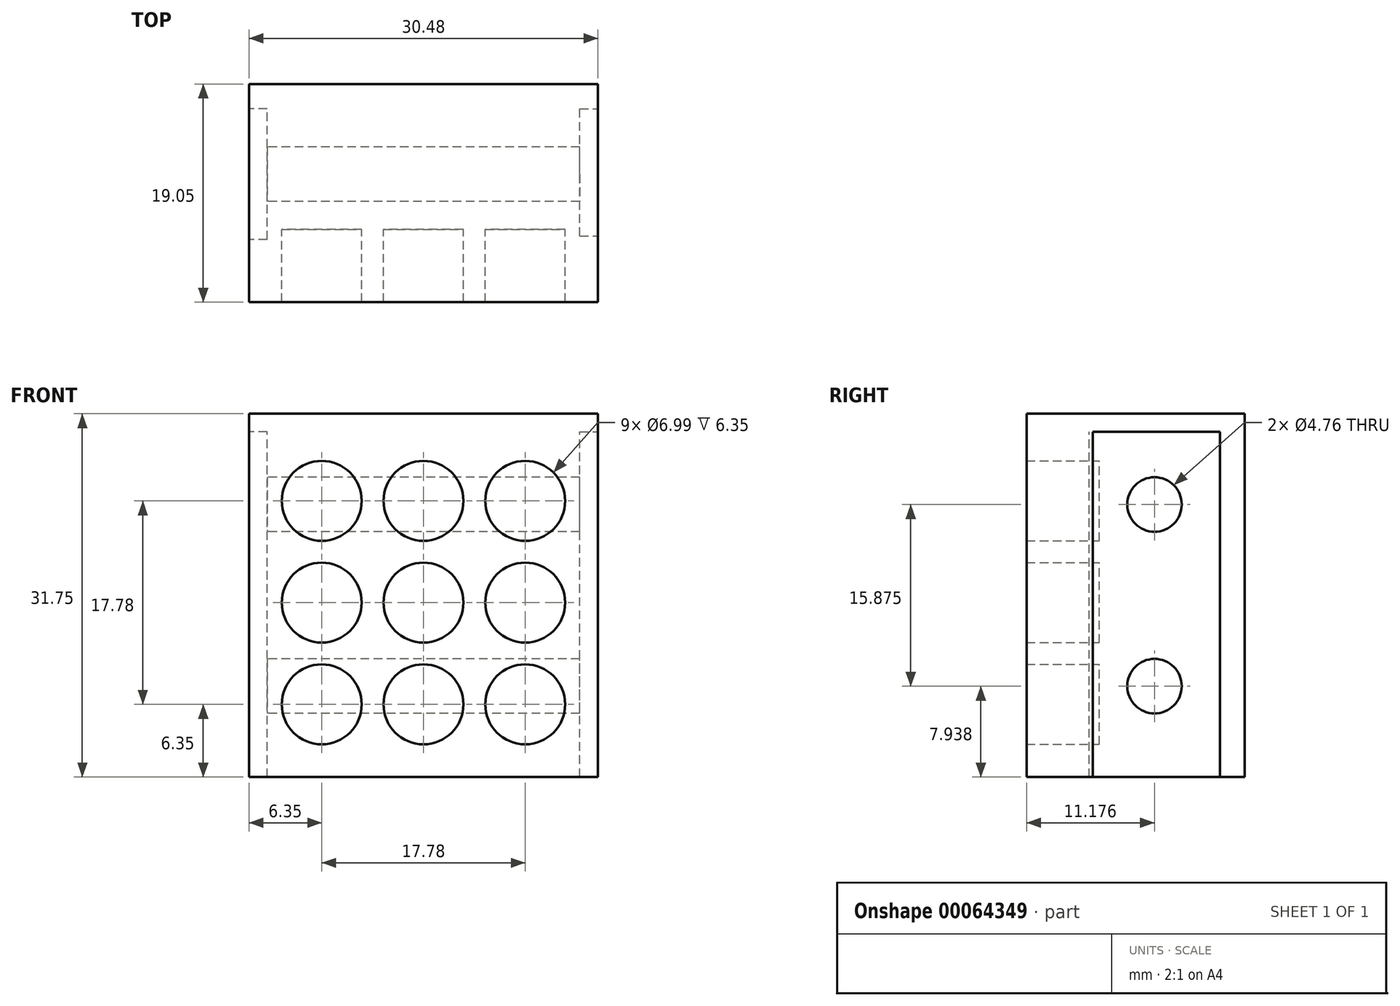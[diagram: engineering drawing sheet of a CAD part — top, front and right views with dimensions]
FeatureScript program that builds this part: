
annotation { "Feature Type Name" : "Feature", "Feature Type Description" : "" }
export const myFeature = defineFeature(function(context is Context, id is Id, definition is map)
    precondition{}
    {
        {
            var Q0;
            Q0=qCreatedBy(makeId("Front.planeOp"),FACE);
            var sketch = newSketch(context, id + "F0", { "sketchPlane" : qUnion([Q0])});
            skLineSegment(sketch, "E0.bottom", {"start": v(0, 0) * mm, "end": v(-30.48, 0) * mm});
            skLineSegment(sketch, "E0.top", {"start": v(0, 31.75) * mm, "end": v(-30.48, 31.75) * mm});
            skLineSegment(sketch, "E0.left", {"start": v(0, 0) * mm, "end": v(0, 31.75) * mm});
            skLineSegment(sketch, "E0.right", {"start": v(-30.48, 0) * mm, "end": v(-30.48, 31.75) * mm});
            skLineSegment(sketch, "E1", {"start": v(-6.35, 31.75) * mm, "end": v(-6.35, 0) * mm, "construction": true});
            skLineSegment(sketch, "E2", {"start": v(-15.24, 31.75) * mm, "end": v(-15.24, 0) * mm, "construction": true});
            skLineSegment(sketch, "E3", {"start": v(-30.48, 24.13) * mm, "end": v(0, 24.13) * mm, "construction": true});
            skLineSegment(sketch, "E4", {"start": v(0, 15.24) * mm, "end": v(-30.48, 15.24) * mm, "construction": true});
            skCircle(sketch, "E5", {"center": v(-6.35, 24.13) * mm, "radius": 3.5 * mm});
            skLineSegment(sketch, "E6", {"start": v(-24.13, 31.75) * mm, "end": v(-24.13, 0) * mm, "construction": true});
            skLineSegment(sketch, "E7", {"start": v(-30.48, 6.35) * mm, "end": v(0, 6.35) * mm, "construction": true});
            skCircle(sketch, "E8.0.1.0", {"center": v(-6.35, 15.24) * mm, "radius": 3.5 * mm});
            skCircle(sketch, "E8.0.2.0", {"center": v(-6.35, 6.35) * mm, "radius": 3.5 * mm});
            skCircle(sketch, "E8.1.0.0", {"center": v(-15.24, 24.13) * mm, "radius": 3.5 * mm});
            skCircle(sketch, "E8.1.1.0", {"center": v(-15.24, 15.24) * mm, "radius": 3.5 * mm});
            skCircle(sketch, "E8.1.2.0", {"center": v(-15.24, 6.35) * mm, "radius": 3.5 * mm});
            skCircle(sketch, "E8.2.0.0", {"center": v(-24.13, 24.13) * mm, "radius": 3.5 * mm});
            skCircle(sketch, "E8.2.1.0", {"center": v(-24.13, 15.24) * mm, "radius": 3.5 * mm});
            skCircle(sketch, "E8.2.2.0", {"center": v(-24.13, 6.35) * mm, "radius": 3.5 * mm});
            skLineSegment(sketch, "E8.direction1", {"start": v(-6.35, 24.13) * mm, "end": v(-15.24, 24.13) * mm, "construction": true});
            skLineSegment(sketch, "E8.direction2", {"start": v(-6.35, 24.13) * mm, "end": v(-6.35, 15.24) * mm, "construction": true});
            skSolve(sketch);
        }
        {
            var Q0;
            Q0=makeQuery(id+"F0.imprint","IMPRINT",FACE,{"disambiguationData":[TD([[makeQuery(id+"F0.imprint","IMPRINT",EDGE,{"derivedFrom":sQuery(id+"F0.wireOp",EDGE,"E0.bottom")}),-1.0]])]});
            extrude(context, id + "F1", {"entities" : qUnion([Q0]), "depth" : 6.35 * mm});
        }
        {
            var Q0;
            Q0=makeQuery(id+"F1.opExtrude","CAP_FACE",FACE,{"disambiguationData":[OSD([sQuery(id+"F0.wireOp",EDGE,"E0.bottom"),sQuery(id+"F0.wireOp",EDGE,"E0.top"),sQuery(id+"F0.wireOp",EDGE,"E0.left"),sQuery(id+"F0.wireOp",EDGE,"E0.right"),sQuery(id+"F0.wireOp",EDGE,"E5"),sQuery(id+"F0.wireOp",EDGE,"E8.0.1.0"),sQuery(id+"F0.wireOp",EDGE,"E8.0.2.0"),sQuery(id+"F0.wireOp",EDGE,"E8.1.0.0"),sQuery(id+"F0.wireOp",EDGE,"E8.1.1.0"),sQuery(id+"F0.wireOp",EDGE,"E8.1.2.0"),sQuery(id+"F0.wireOp",EDGE,"E8.2.0.0"),sQuery(id+"F0.wireOp",EDGE,"E8.2.1.0"),sQuery(id+"F0.wireOp",EDGE,"E8.2.2.0")])],"isStart":true});
            var sketch = newSketch(context, id + "F2", { "sketchPlane" : qUnion([Q0])});
            skLineSegment(sketch, "E9.bottom", {"start": v(0, 31.75) * mm, "end": v(30.48, 31.75) * mm});
            skLineSegment(sketch, "E9.top", {"start": v(0, 0) * mm, "end": v(30.48, 0) * mm});
            skLineSegment(sketch, "E9.left", {"start": v(0, 31.75) * mm, "end": v(0, 0) * mm});
            skLineSegment(sketch, "E9.right", {"start": v(30.48, 31.75) * mm, "end": v(30.48, 0) * mm});
            skSolve(sketch);
        }
        {
            var Q0;
            Q0 = qSketchRegion(id + "F2", true);
            extrude(context, id + "F3", {"entities" : qUnion([Q0]), "operationType" : NewBodyOperationType.ADD, "depth" : 12.7 * mm});
        }
        {
            var Q0;
            Q0=makeQuery(id+"F3.boolean.opBoolean","MERGE",FACE,{"derivedFrom":[makeQuery(id+"F1.opExtrude","SWEPT_FACE",FACE,{"disambiguationData":[OSD([sQuery(id+"F0.wireOp",EDGE,"E0.left")])]}),makeQuery(id+"F3.opExtrude","SWEPT_FACE",FACE,{"disambiguationData":[OSD([sQuery(id+"F2.wireOp",EDGE,"E9.left")])]})]});
            var sketch = newSketch(context, id + "F4", { "sketchPlane" : qUnion([Q0])});
            skLineSegment(sketch, "E10.bottom", {"start": v(-0.57, 0) * mm, "end": v(10.54, 0) * mm});
            skLineSegment(sketch, "E10.top", {"start": v(-0.57, 30.16) * mm, "end": v(10.54, 30.16) * mm});
            skLineSegment(sketch, "E10.left", {"start": v(-0.57, 0) * mm, "end": v(-0.57, 30.16) * mm});
            skLineSegment(sketch, "E10.right", {"start": v(10.54, 0) * mm, "end": v(10.54, 30.16) * mm});
            skSolve(sketch);
        }
        {
            var Q0;
            Q0 = qSketchRegion(id + "F4", true);
            extrude(context, id + "F5", {"entities" : qUnion([Q0]), "operationType" : NewBodyOperationType.REMOVE, "oppositeDirection" : true, "depth" : 1.59 * mm});
        }
        {
            var Q0;
            Q0=makeQuery(id+"F3.boolean.opBoolean","MERGE",FACE,{"derivedFrom":[makeQuery(id+"F1.opExtrude","SWEPT_FACE",FACE,{"disambiguationData":[OSD([sQuery(id+"F0.wireOp",EDGE,"E0.right")])]}),makeQuery(id+"F3.opExtrude","SWEPT_FACE",FACE,{"disambiguationData":[OSD([sQuery(id+"F2.wireOp",EDGE,"E9.right")])]})]});
            var sketch = newSketch(context, id + "F6", { "sketchPlane" : qUnion([Q0])});
            skLineSegment(sketch, "E11.bottom", {"start": v(-10.54, 0) * mm, "end": v(0.89, 0) * mm});
            skLineSegment(sketch, "E11.top", {"start": v(-10.54, 30.16) * mm, "end": v(0.89, 30.16) * mm});
            skLineSegment(sketch, "E11.left", {"start": v(-10.54, 0) * mm, "end": v(-10.54, 30.16) * mm});
            skLineSegment(sketch, "E11.right", {"start": v(0.89, 0) * mm, "end": v(0.89, 30.16) * mm});
            skSolve(sketch);
        }
        {
            var Q0;
            Q0 = qSketchRegion(id + "F6", true);
            extrude(context, id + "F7", {"entities" : qUnion([Q0]), "operationType" : NewBodyOperationType.REMOVE, "oppositeDirection" : true, "depth" : 1.59 * mm});
        }
        {
            var Q0;
            Q0=makeQuery(id+"F7.boolean.opBoolean","COPY",FACE,{"derivedFrom":makeQuery(id+"F7.opExtrude","CAP_FACE",FACE,{"disambiguationData":[OSD([sQuery(id+"F6.wireOp",EDGE,"E11.bottom"),sQuery(id+"F6.wireOp",EDGE,"E11.top"),sQuery(id+"F6.wireOp",EDGE,"E11.left"),sQuery(id+"F6.wireOp",EDGE,"E11.right")])],"isStart":false})});
            var sketch = newSketch(context, id + "F8", { "sketchPlane" : qUnion([Q0])});
            skCircle(sketch, "E12", {"center": v(-4.83, 23.81) * mm, "radius": 2.38 * mm});
            skCircle(sketch, "E13", {"center": v(-4.83, 7.94) * mm, "radius": 2.38 * mm});
            skLineSegment(sketch, "E14", {"start": v(-4.83, 30.16) * mm, "end": v(-4.83, 0) * mm, "construction": true});
            skLineSegment(sketch, "E15", {"start": v(-10.54, 30.16) * mm, "end": v(-10.54, 0) * mm, "construction": true});
            skPoint(sketch, "E16", {"position": v(-4.83, 30.16) * mm});
            skSolve(sketch);
        }
        {
            var Q0;
            Q0 = qSketchRegion(id + "F8", true);
            extrude(context, id + "F9", {"entities" : qUnion([Q0]), "operationType" : NewBodyOperationType.REMOVE, "endBound" : BoundingType.THROUGH_ALL, "oppositeDirection" : true, "depth" : 25.4 * mm});
        }
    });
